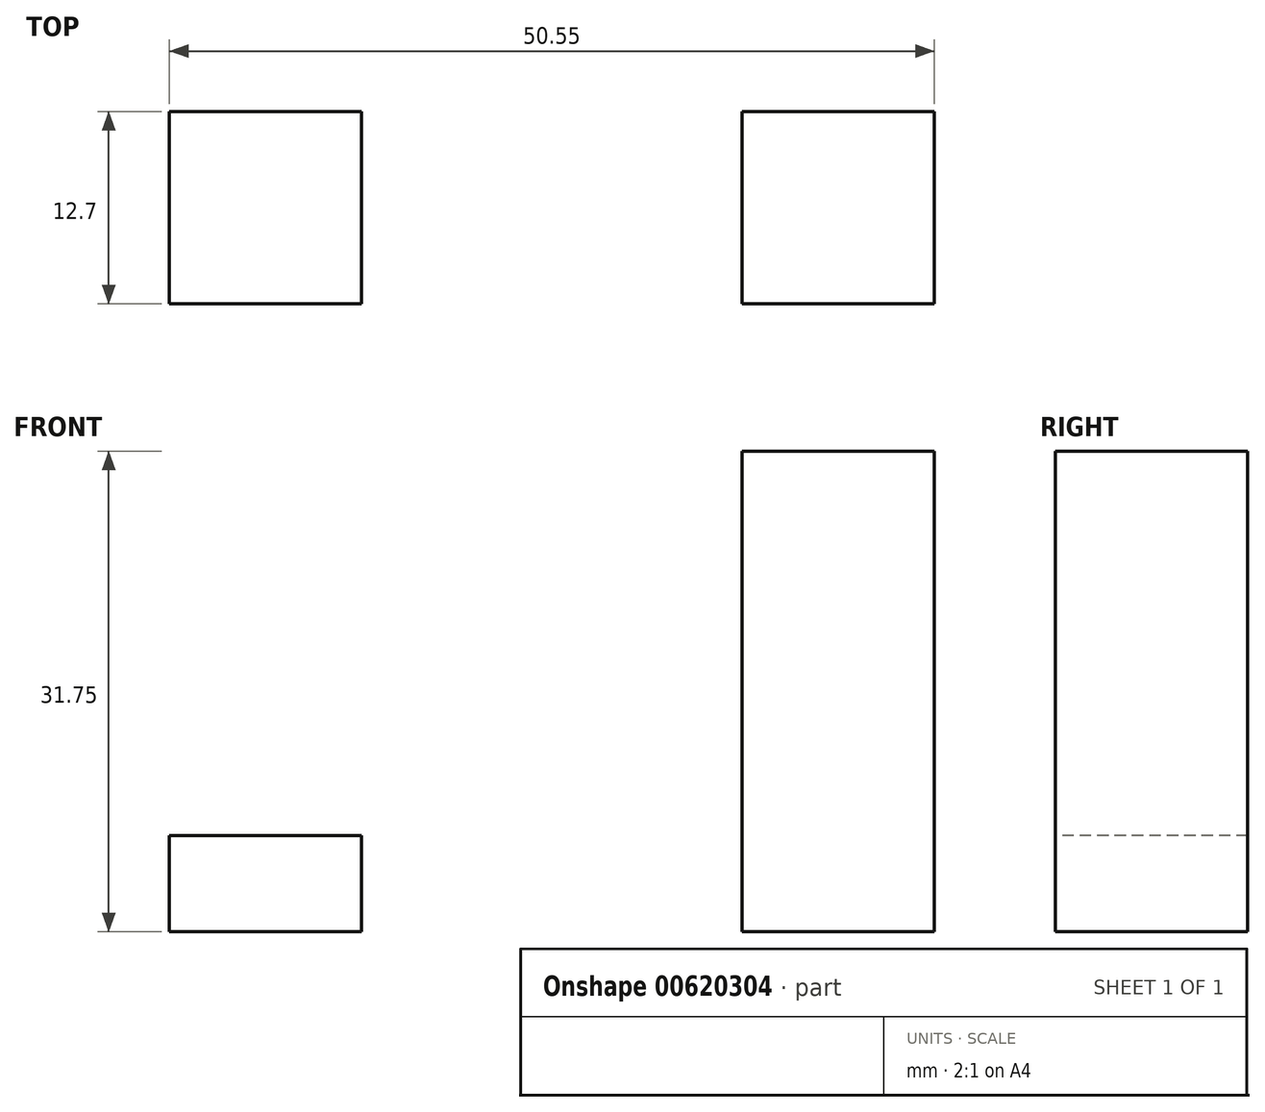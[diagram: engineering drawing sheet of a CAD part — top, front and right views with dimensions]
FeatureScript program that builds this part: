
annotation { "Feature Type Name" : "Feature", "Feature Type Description" : "" }
export const myFeature = defineFeature(function(context is Context, id is Id, definition is map)
    precondition{}
    {
        {
            var Q0;
            Q0=qCreatedBy(makeId("Top.planeOp"),FACE);
            var sketch = newSketch(context, id + "F0", { "sketchPlane" : qUnion([Q0])});
            skLineSegment(sketch, "E0.left", {"start": v(-26.8, 6.17) * mm, "end": v(-26.8, -6.53) * mm});
            skLineSegment(sketch, "E0.right", {"start": v(24, 6.17) * mm, "end": v(24, -6.53) * mm});
            skLineSegment(sketch, "E1.bottom", {"start": v(11.05, 6.17) * mm, "end": v(23.75, 6.17) * mm});
            skLineSegment(sketch, "E1.top", {"start": v(11.05, -6.53) * mm, "end": v(23.75, -6.53) * mm});
            skLineSegment(sketch, "E1.left", {"start": v(11.05, 6.17) * mm, "end": v(11.05, -6.53) * mm});
            skLineSegment(sketch, "E1.right", {"start": v(23.75, 6.17) * mm, "end": v(23.75, -6.53) * mm});
            skLineSegment(sketch, "E2.bottom", {"start": v(-26.8, 6.17) * mm, "end": v(-14.1, 6.17) * mm});
            skLineSegment(sketch, "E2.top", {"start": v(-26.8, -6.53) * mm, "end": v(-14.1, -6.53) * mm});
            skLineSegment(sketch, "E2.right", {"start": v(-14.1, 6.17) * mm, "end": v(-14.1, -6.53) * mm});
            skSolve(sketch);
        }
        {
            var Q0;
            {var subQ2=sQuery(id+"F0.wireOp",EDGE,"E0.left");Q0=makeQuery(id+"F0.imprint","IMPRINT",FACE,{"disambiguationData":[TD([[makeQuery(id+"F0.imprint","IMPRINT",EDGE,{"derivedFrom":subQ2}),1.0]])]});}
            extrude(context, id + "F1", {"entities" : qUnion([Q0]), "depth" : 6.35 * mm, "offsetDistance" : 25.4 * mm});
        }
        {
            var Q0;
            {var subQ0=sQuery(id+"F0.wireOp",EDGE,"E1.left");Q0=makeQuery(id+"F0.imprint","IMPRINT",FACE,{"disambiguationData":[TD([[makeQuery(id+"F0.imprint","IMPRINT",EDGE,{"derivedFrom":subQ0}),1.0]])]});}
            extrude(context, id + "F2", {"entities" : qUnion([Q0]), "operationType" : NewBodyOperationType.ADD, "depth" : 31.75 * mm, "offsetDistance" : 25.4 * mm});
        }
    });
